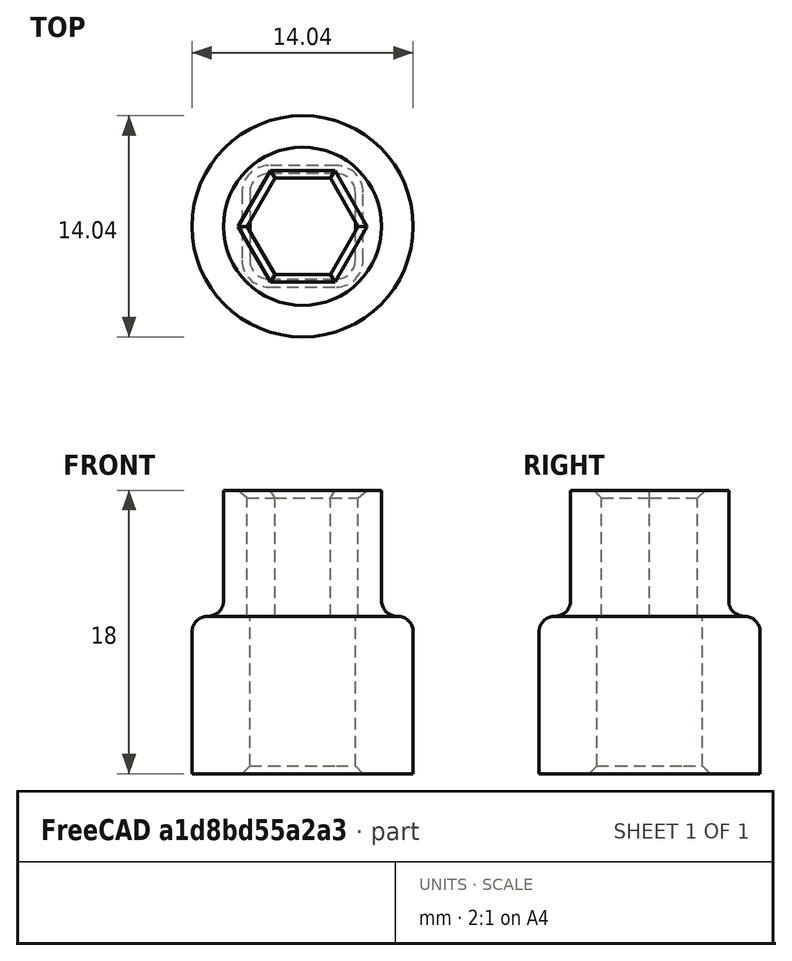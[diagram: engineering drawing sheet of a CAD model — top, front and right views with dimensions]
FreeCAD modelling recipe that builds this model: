
FCSTD DOCUMENT  (FreeCAD 0.17R13519 (Git))
Label: 55socket
License: All rights reserved
LicenseURL: http://en.wikipedia.org/wiki/All_rights_reserved
objects: Sketcher::SketchObject×2, PartDesign::Pad×2, PartDesign::Chamfer×2, PartDesign::Fillet×1, PartDesign::Body×1, Mesh::Feature×1
note: 10 computed .brp shape members not serialized (recipe doc carries the construction recipe); baked Part::Feature solids carry a one-line shape summary decoded from their .brp

FEATURE [Sketcher::SketchObject] Sketch001
  MapMode = 5
  Placement = pos=(0,0,10) rot=(0,0,1;0rad)
  sketch-geometry (9):
    g0: Circle CenterX=0 CenterY=0 CenterZ=0 NormalX=0 NormalY=0 NormalZ=1 AngleXU=0 Radius=5.02184
    g1: LineSegment StartX=1.76092 StartY=-3.05 StartZ=0 EndX=3.52184 EndY=1e-12 EndZ=0
    g2: LineSegment StartX=3.52184 StartY=1e-12 StartZ=0 EndX=1.76092 EndY=3.05 EndZ=0
    g3: LineSegment StartX=1.76092 StartY=3.05 StartZ=0 EndX=-1.76092 EndY=3.05 EndZ=0
    g4: LineSegment StartX=-1.76092 StartY=3.05 StartZ=0 EndX=-3.52184 EndY=-3e-12 EndZ=0
    g5: LineSegment StartX=-3.52184 StartY=-3e-12 StartZ=0 EndX=-1.76092 EndY=-3.05 EndZ=0
    g6: LineSegment StartX=-1.76092 StartY=-3.05 StartZ=0 EndX=1.76092 EndY=-3.05 EndZ=0
    g7: Circle [constr] CenterX=0 CenterY=0 CenterZ=0 NormalX=0 NormalY=0 NormalZ=1 AngleXU=0 Radius=3.52184
    g8: GeomPoint X=5.02184 Y=0 Z=0
  constraints (20):
    c: Coincident(g1,g2)
    c: Coincident(g2,g3)
    c: Coincident(g3,g4)
    c: Coincident(g4,g5)
    c: Coincident(g5,g6)
    c: Coincident(g6,g1)
    c: Equal(g1, g2-g6) x5
    c: PointOnObject(g1,g7)
    c: PointOnObject(g2,g7)
    c: PointOnObject(g3,g7)
    c: PointOnObject(g4,g7)
    c: PointOnObject(g5,g7)
    c: PointOnObject(g6,g7)
    c: Distance(g1,g3) = 6.1
    c: Coincident(g7,g0)
    c: Coincident(g0,g-1)
    c: Horizontal(g6)
    c: PointOnObject(g8,g0)
    c: PointOnObject(g8,g-1)
    c: Distance(g8,g1) = 1.5
FEATURE [Sketcher::SketchObject] Sketch
  ExternalGeometry = -> [Sketch001]
  MapMode = 5
  Support = -> [XY_Plane]
  sketch-geometry (11):
    g0: LineSegment StartX=-2.15 StartY=-3.35 StartZ=0 EndX=2.15 EndY=-3.35 EndZ=0
    g1: LineSegment StartX=3.35 StartY=-2.15 StartZ=0 EndX=3.35 EndY=2.15 EndZ=0
    g2: LineSegment StartX=2.15 StartY=3.35 StartZ=0 EndX=-2.15 EndY=3.35 EndZ=0
    g3: LineSegment StartX=-3.35 StartY=2.15 StartZ=0 EndX=-3.35 EndY=-2.15 EndZ=0
    g4: ArcOfCircle CenterX=-2.15 CenterY=2.15 CenterZ=0 NormalX=0 NormalY=0 NormalZ=1 AngleXU=0 Radius=1.2 StartAngle=1.5708 EndAngle=3.14159
    g5: ArcOfCircle CenterX=2.15 CenterY=2.15 CenterZ=0 NormalX=0 NormalY=0 NormalZ=1 AngleXU=0 Radius=1.2 StartAngle=0 EndAngle=1.5708
    g6: ArcOfCircle CenterX=2.15 CenterY=-2.15 CenterZ=0 NormalX=0 NormalY=0 NormalZ=1 AngleXU=0 Radius=1.2 StartAngle=4.71239 EndAngle=6.28319
    g7: ArcOfCircle CenterX=-2.15 CenterY=-2.15 CenterZ=0 NormalX=0 NormalY=0 NormalZ=1 AngleXU=0 Radius=1.2 StartAngle=3.14159 EndAngle=4.71239
    g8: Circle CenterX=0 CenterY=0 CenterZ=0 NormalX=0 NormalY=0 NormalZ=1 AngleXU=0 Radius=7.02184
    g9: GeomPoint X=-5.02184 Y=0 Z=0
    g10: GeomPoint X=-7.02184 Y=0 Z=0
  constraints (25):
    c: Horizontal(g0)
    c: Horizontal(g2)
    c: Vertical(g1)
    c: Vertical(g3)
    c: Tangent(g3,g4) = -1.5708
    c: Tangent(g2,g4) = -1.5708
    c: Tangent(g2,g5) = -1.5708
    c: Tangent(g1,g5) = -1.5708
    c: Tangent(g1,g6) = -1.5708
    c: Tangent(g0,g6) = -1.5708
    c: Tangent(g0,g7) = -1.5708
    c: Tangent(g3,g7) = -1.5708
    c: Symmetric(g4,g6,g-1)
    c: Radius(g4) = 1.2
    c: Equal(g4,g7)
    c: Equal(g4,g6)
    c: Equal(g4,g5)
    c: Equal(g3,g2)
    c: Coincident(g8,g-1)
    c: Distance(g1,g3) = 6.7
    c: PointOnObject(g9,g-3)
    c: PointOnObject(g9,g-1)
    c: PointOnObject(g10,g-1)
    c: PointOnObject(g10,g8)
    c: Distance(g9,g10) = 2
FEATURE [PartDesign::Pad] Pad
  Length = 10
  Length2 = 100
  Profile = -> Sketch
  Type = 0
FEATURE [PartDesign::Pad] Pad001
  BaseFeature = -> Pad
  Length = 8
  Length2 = 100
  Profile = -> Sketch001
  Type = 0
FEATURE [PartDesign::Fillet] Fillet
  Base = -> Pad001 [Edge12,Edge3]
  BaseFeature = -> Pad001
  Radius = 0.99
FEATURE [PartDesign::Chamfer] Chamfer
  Base = -> Fillet [Edge52,Edge51,Edge55,Edge60,Edge59,Edge56]
  BaseFeature = -> Fillet
  Size = 0.5
FEATURE [PartDesign::Chamfer] Chamfer001
  Base = -> Chamfer [Edge42]
  BaseFeature = -> Chamfer
  Size = 0.5
FEATURE [PartDesign::Body] Body
  Group = -> [Sketch,Sketch001,Pad,Pad001,Fillet,Chamfer,Chamfer001]
  Origin = -> Origin
  Tip = -> Chamfer001
FEATURE [Mesh::Feature] Mesh  label="Body (Meshed)"
